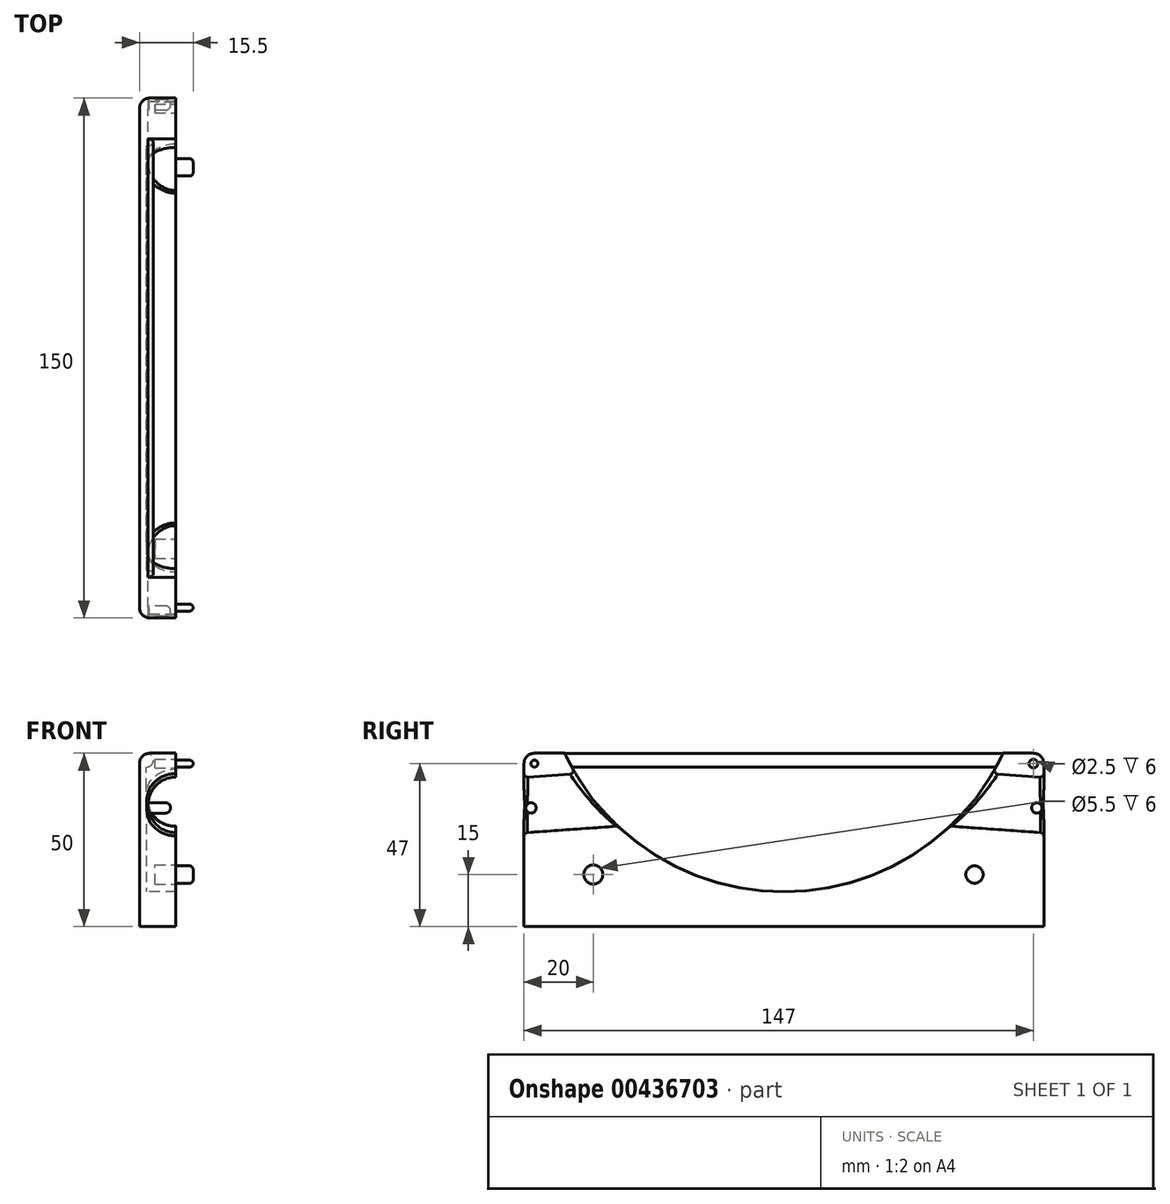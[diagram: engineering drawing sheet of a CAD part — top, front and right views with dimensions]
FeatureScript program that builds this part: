
annotation { "Feature Type Name" : "Feature", "Feature Type Description" : "" }
export const myFeature = defineFeature(function(context is Context, id is Id, definition is map)
    precondition{}
    {
        {
            var Q0;
            Q0=qCreatedBy(makeId("Right.planeOp"),FACE);
            var sketch = newSketch(context, id + "F0", { "sketchPlane" : qUnion([Q0])});
            skCircle(sketch, "E0", {"center": v(0, 0) * mm, "radius": 70 * mm});
            skLineSegment(sketch, "E1.bottom", {"start": v(0, -80) * mm, "end": v(75, -80) * mm});
            skLineSegment(sketch, "E1.top", {"start": v(0, -30) * mm, "end": v(75, -30) * mm});
            skLineSegment(sketch, "E1.left", {"start": v(0, -80) * mm, "end": v(0, -30) * mm});
            skLineSegment(sketch, "E1.right", {"start": v(75, -80) * mm, "end": v(75, -30) * mm});
            skSolve(sketch);
        }
        {
            var Q0;
            {var subQ4=sQuery(id+"F0.wireOp",EDGE,"E1.bottom");Q0=makeQuery(id+"F0.imprint","IMPRINT",FACE,{"disambiguationData":[TD([[makeQuery(id+"F0.imprint","IMPRINT",EDGE,{"derivedFrom":subQ4}),1.0]])]});}
            extrude(context, id + "F1", {"entities" : qUnion([Q0]), "depth" : 8.5 * mm});
        }
        {
            var Q0;
            {var subQ0=makeQuery(id+"F1.opExtrude","CAP_FACE",FACE,{"disambiguationData":[OSD([sQuery(id+"F0.wireOp",EDGE,"E0"),sQuery(id+"F0.wireOp",EDGE,"E1.bottom"),sQuery(id+"F0.wireOp",EDGE,"E1.top"),sQuery(id+"F0.wireOp",EDGE,"E1.left"),sQuery(id+"F0.wireOp",EDGE,"E1.right")])],"isStart":false});Q0=makeQuery(id+"F14.boolean.opBoolean","MERGE",FACE,{"derivedFrom":[subQ0,makeQuery(id+"F14.opPattern","COPY",FACE,{"derivedFrom":subQ0,"instanceName":"1"})]});}
            var sketch = newSketch(context, id + "F2", { "sketchPlane" : qUnion([Q0])});
            skLineSegment(sketch, "E2", {"start": v(25.15, -36.54) * mm, "end": v(85, -40.72) * mm});
            skSolve(sketch);
        }
        {
            var Q0;
            Q0=makeQuery(id+"F1.opExtrude","SWEPT_FACE",FACE,{"disambiguationData":[OSD([sQuery(id+"F0.wireOp",EDGE,"E1.right")])]});
            var sketch = newSketch(context, id + "F3", { "sketchPlane" : qUnion([Q0])});
            skCircle(sketch, "E3", {"center": v(-8.5, -44.95) * mm, "radius": 8 * mm});
            skSolve(sketch);
        }
        {
            var Q0;
            {var subQ0=sQuery(id+"F3.wireOp",EDGE,"E3");var subQ1=makeQuery(id+"F1.opExtrude","CAP_EDGE",EDGE,{"disambiguationData":[OSD([sQuery(id+"F0.wireOp",EDGE,"E1.right")])],"isStart":false});var subQ2=makeQuery(id+"F3.imprint","INTERSECT",VERTEX,{"disambiguationData":[OD(0.0)],"derivedFrom":[subQ1,subQ0]});Q0=makeQuery(id+"F3.imprint","IMPRINT",FACE,{"disambiguationData":[TD([[makeQuery(id+"F3.imprint","IMPRINT",EDGE,{"disambiguationData":[TD([[subQ2,-1.0]])],"derivedFrom":subQ0}),1.0]])]});}
            var Q1;
            {var subQ0=sQuery(id+"F3.wireOp",EDGE,"E3");var subQ1=makeQuery(id+"F1.opExtrude","CAP_EDGE",EDGE,{"disambiguationData":[OSD([sQuery(id+"F0.wireOp",EDGE,"E1.right")])],"isStart":false});var subQ2=makeQuery(id+"F3.imprint","INTERSECT",VERTEX,{"disambiguationData":[OD(0.0)],"derivedFrom":[subQ1,subQ0]});Q1=makeQuery(id+"F3.imprint","IMPRINT",FACE,{"disambiguationData":[TD([[makeQuery(id+"F3.imprint","IMPRINT",EDGE,{"disambiguationData":[TD([[subQ2,1.0]])],"derivedFrom":subQ0}),1.0]])]});}
            var Q2;
            Q2=sQuery(id+"F2.wireOp",EDGE,"E2");
            sweep(context, id + "F4", {"operationType" : NewBodyOperationType.REMOVE, "profiles" : qUnion([Q0, Q1]), "path" : qUnion([Q2])});
        }
        {
            var Q0;
            Q0=makeQuery(id+"F4.boolean.opBoolean","INTERSECT",EDGE,{"derivedFrom":[makeQuery(id+"F1.opExtrude","SWEPT_FACE",FACE,{"disambiguationData":[OSD([sQuery(id+"F0.wireOp",EDGE,"E0")])]}),makeQuery(id+"F4.opSweep","SWEPT_FACE",FACE,{"disambiguationData":[OSD([sQuery(id+"F2.wireOp",EDGE,"E2"),sQuery(id+"F3.wireOp",EDGE,"E3")])]})]});
            var Q1;
            Q1=makeQuery(id+"F4.boolean.opBoolean","INTERSECT",EDGE,{"derivedFrom":[makeQuery(id+"F1.opExtrude","SWEPT_FACE",FACE,{"disambiguationData":[OSD([sQuery(id+"F0.wireOp",EDGE,"E1.right")])]}),makeQuery(id+"F4.opSweep","SWEPT_FACE",FACE,{"disambiguationData":[OSD([sQuery(id+"F2.wireOp",EDGE,"E2"),sQuery(id+"F3.wireOp",EDGE,"E3")])]})]});
            fillet(context, id + "F5", {"entities" : qUnion([Q0, Q1]), "radius" : 1 * mm, "tangentPropagation" : true, "allowEdgeOverflow" : false});
        }
        {
            var Q0;
            Q0=makeQuery(id+"F1.opExtrude","CAP_FACE",FACE,{"disambiguationData":[OSD([sQuery(id+"F0.wireOp",EDGE,"E0"),sQuery(id+"F0.wireOp",EDGE,"E1.bottom"),sQuery(id+"F0.wireOp",EDGE,"E1.top"),sQuery(id+"F0.wireOp",EDGE,"E1.left"),sQuery(id+"F0.wireOp",EDGE,"E1.right")])],"isStart":true});
            var sketch = newSketch(context, id + "F6", { "sketchPlane" : qUnion([Q0])});
            skCircle(sketch, "E4", {"center": v(-73, -45.79) * mm, "radius": 1.5 * mm});
            skSolve(sketch);
        }
        {
            var Q0;
            Q0=makeQuery(id+"F6.imprint","IMPRINT",FACE,{"disambiguationData":[TD([[makeQuery(id+"F6.imprint","IMPRINT",EDGE,{"derivedFrom":sQuery(id+"F6.wireOp",EDGE,"E4")}),1.0]])]});
            extrude(context, id + "F7", {"entities" : qUnion([Q0]), "operationType" : NewBodyOperationType.ADD, "oppositeDirection" : true, "depth" : 7 * mm});
        }
        {
            var Q0;
            Q0=makeQuery(id+"F7.opExtrude","CAP_EDGE",EDGE,{"disambiguationData":[OSD([sQuery(id+"F6.wireOp",EDGE,"E4")])],"isStart":false});
            fillet(context, id + "F8", {"entities" : qUnion([Q0]), "radius" : 1.5 * mm, "tangentPropagation" : true, "allowEdgeOverflow" : false});
        }
        {
            var Q0;
            Q0=makeQuery(id+"F1.opExtrude","CAP_FACE",FACE,{"disambiguationData":[OSD([sQuery(id+"F0.wireOp",EDGE,"E0"),sQuery(id+"F0.wireOp",EDGE,"E1.bottom"),sQuery(id+"F0.wireOp",EDGE,"E1.top"),sQuery(id+"F0.wireOp",EDGE,"E1.left"),sQuery(id+"F0.wireOp",EDGE,"E1.right")])],"isStart":true});
            var sketch = newSketch(context, id + "F9", { "sketchPlane" : qUnion([Q0])});
            skLineSegment(sketch, "E5.bottom", {"start": v(-75, -30) * mm, "end": v(0, -30) * mm});
            skLineSegment(sketch, "E5.top", {"start": v(-75, -80) * mm, "end": v(0, -80) * mm});
            skLineSegment(sketch, "E5.left", {"start": v(-75, -30) * mm, "end": v(-75, -80) * mm});
            skLineSegment(sketch, "E5.right", {"start": v(0, -30) * mm, "end": v(0, -80) * mm});
            skSolve(sketch);
        }
        {
            var Q0;
            Q0=makeQuery(id+"F9.imprint","IMPRINT",FACE,{"disambiguationData":[TD([[makeQuery(id+"F9.imprint","IMPRINT",EDGE,{"derivedFrom":sQuery(id+"F9.wireOp",EDGE,"E5.top")}),-1.0]])]});
            var Q1;
            {var subQ1=makeQuery(id+"F1.opExtrude","CAP_EDGE",EDGE,{"disambiguationData":[OSD([sQuery(id+"F0.wireOp",EDGE,"E0")])],"isStart":true});var subQ2=makeQuery(id+"F14.boolean.opBoolean","MERGE",EDGE,{"derivedFrom":[subQ1,makeQuery(id+"F14.opPattern","COPY",EDGE,{"derivedFrom":subQ1,"instanceName":"1"})]});Q1=makeQuery(id+"F9.imprint","IMPRINT",FACE,{"disambiguationData":[TD([[makeQuery(id+"F9.imprint","IMPRINT",EDGE,{"derivedFrom":subQ2}),-1.0]])]});}
            extrude(context, id + "F10", {"entities" : qUnion([Q0, Q1]), "operationType" : NewBodyOperationType.ADD, "depth" : 2 * mm});
        }
        {
            var Q0;
            Q0=makeQuery(id+"F10.boolean.opBoolean","MERGE",FACE,{"derivedFrom":[makeQuery(id+"F1.opExtrude","SWEPT_FACE",FACE,{"disambiguationData":[OSD([sQuery(id+"F0.wireOp",EDGE,"E1.right")])]}),makeQuery(id+"F10.opExtrude","SWEPT_FACE",FACE,{"disambiguationData":[OSD([sQuery(id+"F9.wireOp",EDGE,"E5.left")])]})]});
            var sketch = newSketch(context, id + "F11", { "sketchPlane" : qUnion([Q0])});
            skCircle(sketch, "E6", {"center": v(0, -32) * mm, "radius": 2 * mm});
            skSolve(sketch);
        }
        {
            var Q0;
            Q0=makeQuery(id+"F11.imprint","IMPRINT",FACE,{"disambiguationData":[TD([[makeQuery(id+"F11.imprint","IMPRINT",EDGE,{"derivedFrom":sQuery(id+"F11.wireOp",EDGE,"E6")}),1.0]])]});
            var Q1;
            Q1=makeQuery(id+"F10.opExtrude","CAP_EDGE",EDGE,{"disambiguationData":[OSD([sQuery(id+"F9.wireOp",EDGE,"E5.bottom")])],"isStart":false});
            sweep(context, id + "F12", {"operationType" : NewBodyOperationType.ADD, "profiles" : qUnion([Q0]), "path" : qUnion([Q1]), "keepProfileOrientation" : true});
        }
        {
            var Q0;
            Q0=makeQuery(id+"F10.opExtrude","CAP_EDGE",EDGE,{"disambiguationData":[OSD([sQuery(id+"F9.wireOp",EDGE,"E5.bottom")])],"isStart":false});
            var Q1;
            Q1=makeQuery(id+"F10.opExtrude","CAP_EDGE",EDGE,{"disambiguationData":[OSD([sQuery(id+"F9.wireOp",EDGE,"E5.left")])],"isStart":false});
            var Q2;
            Q2=makeQuery(id+"F10.boolean.opBoolean","MERGE",EDGE,{"derivedFrom":[makeQuery(id+"F1.opExtrude","SWEPT_EDGE",EDGE,{"disambiguationData":[OSD([sQuery(id+"F0.wireOp",EDGE,"E1.top"),sQuery(id+"F0.wireOp",EDGE,"E1.right")])]}),makeQuery(id+"F10.opExtrude","SWEPT_EDGE",EDGE,{"disambiguationData":[OSD([sQuery(id+"F9.wireOp",EDGE,"E5.bottom"),sQuery(id+"F9.wireOp",EDGE,"E5.left")])]})]});
            fillet(context, id + "F13", {"entities" : qUnion([Q0, Q1, Q2]), "radius" : 3 * mm, "tangentPropagation" : true, "allowEdgeOverflow" : false});
        }
        {
            var Q0;
            Q0=makeQuery(id+"F1.opExtrude","SWEPT_BODY",BODY,{"disambiguationData":[OSD([sQuery(id+"F0.wireOp",EDGE,"E0"),sQuery(id+"F0.wireOp",EDGE,"E1.bottom"),sQuery(id+"F0.wireOp",EDGE,"E1.top"),sQuery(id+"F0.wireOp",EDGE,"E1.left"),sQuery(id+"F0.wireOp",EDGE,"E1.right")])]});
            var Q1;
            Q1=qCreatedBy(makeId("Front.planeOp"),FACE);
            mirror(context, id + "F14", {"operationType" : NewBodyOperationType.ADD, "entities" : qUnion([Q0]), "mirrorPlane" : qUnion([Q1])});
        }
        {
            var Q0;
            {var subQ0=sQuery(id+"F0.wireOp",EDGE,"E0");var subQ1=sQuery(id+"F0.wireOp",EDGE,"E1.top");var subQ2=sQuery(id+"F0.wireOp",EDGE,"E1.right");Q0=makeQuery(id+"F4.boolean.opBoolean","SPLIT",FACE,{"disambiguationData":[TD([makeQuery(id+"F1.opExtrude","SWEPT_FACE",FACE,{"disambiguationData":[OSD([subQ1])]})])],"derivedFrom":makeQuery(id+"F1.opExtrude","CAP_FACE",FACE,{"disambiguationData":[OSD([subQ0,sQuery(id+"F0.wireOp",EDGE,"E1.bottom"),subQ1,sQuery(id+"F0.wireOp",EDGE,"E1.left"),subQ2])],"isStart":false})});}
            var sketch = newSketch(context, id + "F15", { "sketchPlane" : qUnion([Q0])});
            skCircle(sketch, "E7", {"center": v(55, -65) * mm, "radius": 2.5 * mm});
            skCircle(sketch, "E8", {"center": v(-55, -65) * mm, "radius": 2.75 * mm});
            skLineSegment(sketch, "E9.bottom", {"start": v(-75, -25) * mm, "end": v(75, -25) * mm, "construction": true});
            skLineSegment(sketch, "E9.top", {"start": v(-75, -80) * mm, "end": v(75, -80) * mm, "construction": true});
            skLineSegment(sketch, "E9.left", {"start": v(-75, -25) * mm, "end": v(-75, -80) * mm, "construction": true});
            skLineSegment(sketch, "E9.right", {"start": v(75, -25) * mm, "end": v(75, -80) * mm, "construction": true});
            skLineSegment(sketch, "E10", {"start": v(-55, -65) * mm, "end": v(-55, -80) * mm, "construction": true});
            skLineSegment(sketch, "E11", {"start": v(-55, -65) * mm, "end": v(-75, -65) * mm, "construction": true});
            skLineSegment(sketch, "E12", {"start": v(55, -65) * mm, "end": v(75, -65) * mm, "construction": true});
            skLineSegment(sketch, "E13", {"start": v(55, -65) * mm, "end": v(55, -80) * mm, "construction": true});
            skCircle(sketch, "E14", {"center": v(72, -33) * mm, "radius": 1.25 * mm});
            skLineSegment(sketch, "E15", {"start": v(72, -33) * mm, "end": v(72, -80) * mm, "construction": true});
            skCircle(sketch, "E16", {"center": v(-72, -33) * mm, "radius": 1 * mm});
            skLineSegment(sketch, "E17", {"start": v(-72, -33) * mm, "end": v(-72, -80) * mm, "construction": true});
            skLineSegment(sketch, "E18", {"start": v(72, -33) * mm, "end": v(75, -33) * mm, "construction": true});
            skLineSegment(sketch, "E19", {"start": v(-72, -33) * mm, "end": v(-75, -33) * mm, "construction": true});
            skSolve(sketch);
        }
        {
            var Q0;
            Q0=makeQuery(id+"F15.imprint","IMPRINT",FACE,{"disambiguationData":[TD([[makeQuery(id+"F15.imprint","IMPRINT",EDGE,{"derivedFrom":sQuery(id+"F15.wireOp",EDGE,"E7")}),1.0]])]});
            var Q1;
            Q1=makeQuery(id+"F15.imprint","IMPRINT",FACE,{"disambiguationData":[TD([[makeQuery(id+"F15.imprint","IMPRINT",EDGE,{"derivedFrom":sQuery(id+"F15.wireOp",EDGE,"E16")}),1.0]])]});
            extrude(context, id + "F16", {"entities" : qUnion([Q0, Q1]), "operationType" : NewBodyOperationType.ADD, "depth" : 5 * mm});
        }
        {
            var Q0;
            Q0=makeQuery(id+"F15.imprint","IMPRINT",FACE,{"disambiguationData":[TD([[makeQuery(id+"F15.imprint","IMPRINT",EDGE,{"derivedFrom":sQuery(id+"F15.wireOp",EDGE,"E8")}),1.0]])]});
            var Q1;
            Q1=makeQuery(id+"F15.imprint","IMPRINT",FACE,{"disambiguationData":[TD([[makeQuery(id+"F15.imprint","IMPRINT",EDGE,{"derivedFrom":sQuery(id+"F15.wireOp",EDGE,"E14")}),1.0]])]});
            extrude(context, id + "F17", {"entities" : qUnion([Q0, Q1]), "operationType" : NewBodyOperationType.REMOVE, "oppositeDirection" : true, "depth" : 6 * mm});
        }
        {
            var Q0;
            Q0=makeQuery(id+"F17.boolean.opBoolean","COPY",EDGE,{"derivedFrom":makeQuery(id+"F17.opExtrude","CAP_EDGE",EDGE,{"disambiguationData":[OSD([sQuery(id+"F15.wireOp",EDGE,"E8")])],"isStart":true})});
            var Q1;
            Q1=makeQuery(id+"F16.opExtrude","CAP_EDGE",EDGE,{"disambiguationData":[OSD([sQuery(id+"F15.wireOp",EDGE,"E7")])],"isStart":false});
            var Q2;
            Q2=makeQuery(id+"F16.opExtrude","CAP_EDGE",EDGE,{"disambiguationData":[OSD([sQuery(id+"F15.wireOp",EDGE,"E16")])],"isStart":false});
            var Q3;
            Q3=makeQuery(id+"F17.boolean.opBoolean","COPY",EDGE,{"derivedFrom":makeQuery(id+"F17.opExtrude","CAP_EDGE",EDGE,{"disambiguationData":[OSD([sQuery(id+"F15.wireOp",EDGE,"E14")])],"isStart":true})});
            fillet(context, id + "F18", {"entities" : qUnion([Q0, Q1, Q2, Q3]), "radius" : 1 * mm, "tangentPropagation" : true, "allowEdgeOverflow" : false});
        }
    });
